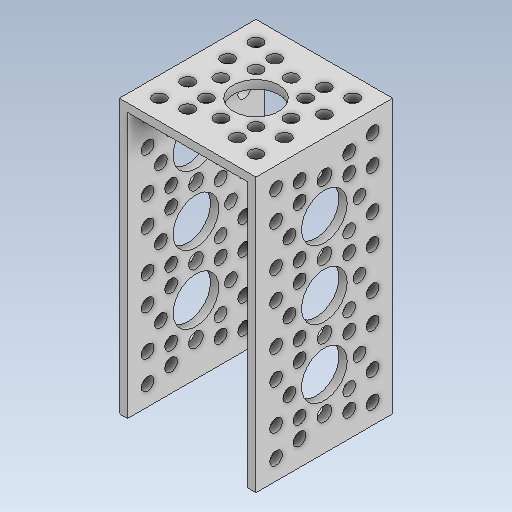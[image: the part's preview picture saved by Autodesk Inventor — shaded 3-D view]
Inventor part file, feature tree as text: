
AUTODESK INVENTOR PART (.ipt)
format: ipt  version: 2020 (Build 240168000, 168)  size: 303,104 bytes
history: native  units: in
note: dims shown in document units (in); Inventor stores cm internally (conversion verified against a paired STEP export)
features: mirror x1
ambient origin geometry x8: Origin, YZ Plane, XZ Plane, XY Plane, X Axis, Y Axis, Z Axis, Center Point
bodies: Solid1 (feature_tree)
feature tree (1):
  mirror  "Mirror4"
